# Revit family: Backwater_Valve_7012_JRSmith
name_source: partatom
category: Plumbing Fixtures
revit_build: Autodesk Revit MEP 2012 (Build: 20110309_2315(x64)
units: mm (PartAtom-declared; Revit-internal decimal feet)

## types (6) — shared parameters
04 CSI = 22 05 23
95 CSI = 15110
Action = Flapper
Assembly Code = D2030400
Default Elevation = 48"
Description = Duco cast iron body with backwater valve
Manufacturer = Jay R. Smith Mfg. Co.
Manufacturer's URL = http://JRSmith.com
Material = Cast Iron
Material Finish = Duco Coated
Model = 7012
OmniClass Code = 22-22 13 19 33
OmniClass Title = Backwater Valves
Product URL = http://www.jrsmith.com
SMARTBIM URL = www.smartbim.com
SmartBIM Object Version = 3
URL = http://www.jrsmith.com
Warranty = 1 year material and workmanship

## per-type parameters (varying)
| type | A Radius | B | C | Caulk Connection | D | F Diameter | F Radius | G | Lower Pipe Offset | No Hub Connection | Outlet Diameter | Threaded Connection | Top Plate Radius | Weight (lb) |
| 7012-08 | 4" | 9 1/2" | 9 1/2" | Yes | 12 1/2" | 13" | 6 1/2" | 11 3/4" | 4 1/4" | Yes | 8" | Yes | 6 3/8" | 102.5 |
| 7012-04 | 2" | 6 1/2" | 6 1/2" | No | 9 1/2" | 8 1/2" | 4 1/4" | 8" | 2 1/4" | No | 4" | No | 4 1/8" | 28.82 |
| 7012-03 | 1 1/2" | 6 1/4" | 5 3/4" | No | 9" | 7 1/2" | 3 3/4" | 6" | 1 3/4" | No | 3" | No | 3 5/8" | 22.09 |
| 7012-05 | 2 1/2" | 7" | 7 3/4" | No | 10 1/2" | 10 3/4" | 5 3/8" | 8 3/4" | 2 3/4" | No | 5" | No | 5 1/4" | 55.63 |
| 7012-06 | 3" | 8" | 7 3/4" | No | 11 1/2" | 10 3/4" | 5 3/8" | 9 3/4" | 3 1/4" | No | 6" | No | 5 1/4" | 56 |
| 7012-02 | 1" | 4 1/2" | 5" | No | 7" | 6 1/2" | 3 1/4" | 6" | 1 1/4" | No | 2" | No | 3 1/8" | 12.84 |

## geometry (parser evidence)
native form markers: Blend x8, Sweep x11
no freeform markers — native parametric forms only
